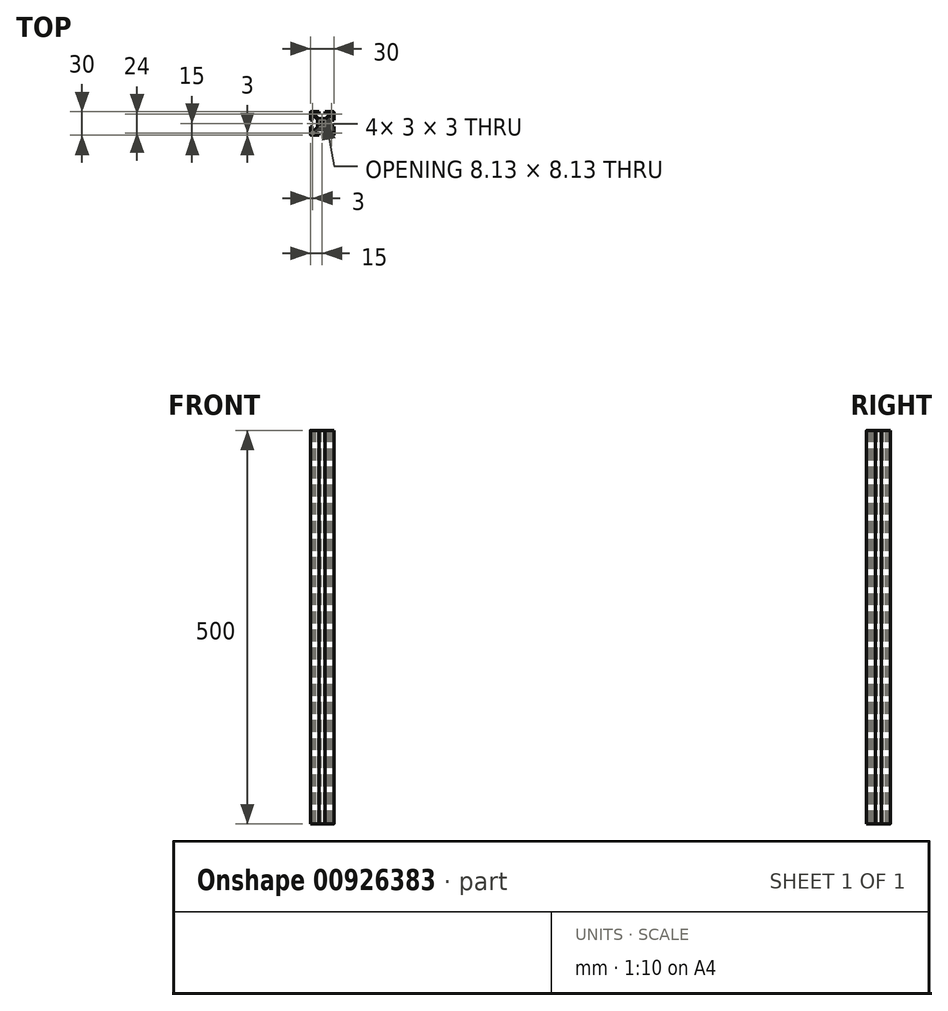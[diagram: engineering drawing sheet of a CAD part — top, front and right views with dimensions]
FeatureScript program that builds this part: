
annotation { "Feature Type Name" : "Feature", "Feature Type Description" : "" }
export const myFeature = defineFeature(function(context is Context, id is Id, definition is map)
    precondition{}
    {
        {
            var Q0;
            Q0=qCreatedBy(makeId("Top.planeOp"),FACE);
            var sketch = newSketch(context, id + "F0", { "sketchPlane" : qUnion([Q0])});
            skLineSegment(sketch, "E0", {"start": v(0, 0) * mm, "end": v(11, 0) * mm});
            skLineSegment(sketch, "E1", {"start": v(11, 0) * mm, "end": v(11, 2) * mm});
            skLineSegment(sketch, "E2", {"start": v(11, 2) * mm, "end": v(6, 2) * mm});
            skLineSegment(sketch, "E3", {"start": v(6, 2) * mm, "end": v(6, 4.59) * mm});
            skLineSegment(sketch, "E4", {"start": v(6, 4.59) * mm, "end": v(10.41, 9) * mm});
            skLineSegment(sketch, "E5", {"start": v(10.41, 9) * mm, "end": v(15, 9) * mm});
            skLineSegment(sketch, "E6", {"start": v(0, 0) * mm, "end": v(33.2, 33.2) * mm, "construction": true});
            skLineSegment(sketch, "E7", {"start": v(0, 15) * mm, "end": v(36.66, 15) * mm, "construction": true});
            skLineSegment(sketch, "E8", {"start": v(15, 0) * mm, "end": v(15, 32.9) * mm, "construction": true});
            skLineSegment(sketch, "E9", {"start": v(1.5, 1.5) * mm, "end": v(4.5, 1.5) * mm});
            skLineSegment(sketch, "E10", {"start": v(4.5, 1.5) * mm, "end": v(4.5, 4.5) * mm});
            skArc(sketch, "E11", {"start": v(13.19, 12.12) * mm, "mid": v(14.06, 11.73) * mm, "end": v(15, 11.6) * mm});
            skLineSegment(sketch, "E12", {"start": v(13.19, 12.12) * mm, "end": v(12, 10.93) * mm});
            skLineSegment(sketch, "E13", {"start": v(12, 10.93) * mm, "end": v(11.46, 11.46) * mm});
            skArc(sketch, "E14.MirrorCS", {"start": v(12.12, 13.19) * mm, "mid": v(11.73, 14.06) * mm, "end": v(11.6, 15) * mm});
            skLineSegment(sketch, "E15.MirrorCS", {"start": v(12.12, 13.19) * mm, "end": v(10.93, 12) * mm});
            skLineSegment(sketch, "E16.MirrorCS", {"start": v(10.93, 12) * mm, "end": v(11.46, 11.46) * mm});
            skLineSegment(sketch, "E17.MirrorCS", {"start": v(9, 10.41) * mm, "end": v(9, 15) * mm});
            skLineSegment(sketch, "E18.MirrorCS", {"start": v(4.59, 6) * mm, "end": v(9, 10.41) * mm});
            skLineSegment(sketch, "E19.MirrorCS", {"start": v(1.5, 4.5) * mm, "end": v(4.5, 4.5) * mm});
            skLineSegment(sketch, "E20.MirrorCS", {"start": v(1.5, 1.5) * mm, "end": v(1.5, 4.5) * mm});
            skLineSegment(sketch, "E21.MirrorCS", {"start": v(2, 11) * mm, "end": v(2, 6) * mm});
            skLineSegment(sketch, "E22.MirrorCS", {"start": v(0, 0) * mm, "end": v(0, 11) * mm});
            skLineSegment(sketch, "E23.MirrorCS", {"start": v(0, 11) * mm, "end": v(2, 11) * mm});
            skLineSegment(sketch, "E24.MirrorCS", {"start": v(2, 6) * mm, "end": v(4.59, 6) * mm});
            skLineSegment(sketch, "E25.MirrorCS", {"start": v(10.93, 18) * mm, "end": v(11.46, 18.54) * mm});
            skLineSegment(sketch, "E26.MirrorCS", {"start": v(12, 19.07) * mm, "end": v(11.46, 18.54) * mm});
            skLineSegment(sketch, "E27.MirrorCS", {"start": v(13.19, 17.88) * mm, "end": v(12, 19.07) * mm});
            skLineSegment(sketch, "E28.MirrorCS", {"start": v(11, 28) * mm, "end": v(6, 28) * mm});
            skLineSegment(sketch, "E29.MirrorCS", {"start": v(2, 19) * mm, "end": v(2, 24) * mm});
            skLineSegment(sketch, "E30.MirrorCS", {"start": v(12.12, 16.81) * mm, "end": v(10.93, 18) * mm});
            skLineSegment(sketch, "E31.MirrorCS", {"start": v(2, 24) * mm, "end": v(4.59, 24) * mm});
            skLineSegment(sketch, "E32.MirrorCS", {"start": v(4.59, 24) * mm, "end": v(9, 19.59) * mm});
            skLineSegment(sketch, "E33.MirrorCS", {"start": v(1.5, 28.5) * mm, "end": v(4.5, 28.5) * mm});
            skLineSegment(sketch, "E34.MirrorCS", {"start": v(0, 30) * mm, "end": v(0, 19) * mm});
            skLineSegment(sketch, "E35.MirrorCS", {"start": v(1.5, 28.5) * mm, "end": v(1.5, 25.5) * mm});
            skLineSegment(sketch, "E36.MirrorCS", {"start": v(10.41, 21) * mm, "end": v(15, 21) * mm});
            skArc(sketch, "E37.MirrorCS", {"start": v(13.19, 17.88) * mm, "mid": v(14.06, 18.27) * mm, "end": v(15, 18.4) * mm});
            skLineSegment(sketch, "E38.MirrorCS", {"start": v(1.5, 25.5) * mm, "end": v(4.5, 25.5) * mm});
            skLineSegment(sketch, "E39.MirrorCS", {"start": v(0, 19) * mm, "end": v(2, 19) * mm});
            skArc(sketch, "E40.MirrorCS", {"start": v(12.12, 16.81) * mm, "mid": v(11.73, 15.94) * mm, "end": v(11.6, 15) * mm});
            skLineSegment(sketch, "E41.MirrorCS", {"start": v(11, 30) * mm, "end": v(11, 28) * mm});
            skLineSegment(sketch, "E42.MirrorCS", {"start": v(6, 25.41) * mm, "end": v(10.41, 21) * mm});
            skLineSegment(sketch, "E43.MirrorCS", {"start": v(4.5, 28.5) * mm, "end": v(4.5, 25.5) * mm});
            skLineSegment(sketch, "E44.MirrorCS", {"start": v(6, 28) * mm, "end": v(6, 25.41) * mm});
            skLineSegment(sketch, "E45.MirrorCS", {"start": v(0, 30) * mm, "end": v(11, 30) * mm});
            skLineSegment(sketch, "E46.MirrorCS", {"start": v(9, 19.59) * mm, "end": v(9, 15) * mm});
            skLineSegment(sketch, "E47.MirrorCS", {"start": v(18, 10.93) * mm, "end": v(18.54, 11.46) * mm});
            skLineSegment(sketch, "E48.MirrorCS", {"start": v(16.81, 17.88) * mm, "end": v(18, 19.07) * mm});
            skLineSegment(sketch, "E49.MirrorCS", {"start": v(19.07, 18) * mm, "end": v(18.54, 18.54) * mm});
            skLineSegment(sketch, "E50.MirrorCS", {"start": v(17.88, 16.81) * mm, "end": v(19.07, 18) * mm});
            skLineSegment(sketch, "E51.MirrorCS", {"start": v(17.88, 13.19) * mm, "end": v(19.07, 12) * mm});
            skLineSegment(sketch, "E52.MirrorCS", {"start": v(16.81, 12.12) * mm, "end": v(18, 10.93) * mm});
            skLineSegment(sketch, "E53.MirrorCS", {"start": v(18, 19.07) * mm, "end": v(18.54, 18.54) * mm});
            skLineSegment(sketch, "E54.MirrorCS", {"start": v(19.07, 12) * mm, "end": v(18.54, 11.46) * mm});
            skLineSegment(sketch, "E55.MirrorCS", {"start": v(25.5, 1.5) * mm, "end": v(25.5, 4.5) * mm});
            skLineSegment(sketch, "E56.MirrorCS", {"start": v(24, 2) * mm, "end": v(24, 4.59) * mm});
            skLineSegment(sketch, "E57.MirrorCS", {"start": v(24, 4.59) * mm, "end": v(19.59, 9) * mm});
            skLineSegment(sketch, "E58.MirrorCS", {"start": v(24, 25.41) * mm, "end": v(19.59, 21) * mm});
            skLineSegment(sketch, "E59.MirrorCS", {"start": v(24, 28) * mm, "end": v(24, 25.41) * mm});
            skArc(sketch, "E60.MirrorCS", {"start": v(17.88, 13.19) * mm, "mid": v(18.27, 14.06) * mm, "end": v(18.4, 15) * mm});
            skArc(sketch, "E61.MirrorCS", {"start": v(16.81, 17.88) * mm, "mid": v(15.94, 18.27) * mm, "end": v(15, 18.4) * mm});
            skLineSegment(sketch, "E62.MirrorCS", {"start": v(28, 24) * mm, "end": v(25.41, 24) * mm});
            skLineSegment(sketch, "E63.MirrorCS", {"start": v(25.5, 28.5) * mm, "end": v(25.5, 25.5) * mm});
            skLineSegment(sketch, "E64.MirrorCS", {"start": v(28.5, 1.5) * mm, "end": v(28.5, 4.5) * mm});
            skLineSegment(sketch, "E65.MirrorCS", {"start": v(21, 10.41) * mm, "end": v(21, 15) * mm});
            skLineSegment(sketch, "E66.MirrorCS", {"start": v(28, 11) * mm, "end": v(28, 6) * mm});
            skLineSegment(sketch, "E67.MirrorCS", {"start": v(21, 19.59) * mm, "end": v(21, 15) * mm});
            skLineSegment(sketch, "E68.MirrorCS", {"start": v(30, 0) * mm, "end": v(19, 0) * mm});
            skArc(sketch, "E69.MirrorCS", {"start": v(17.88, 16.81) * mm, "mid": v(18.27, 15.94) * mm, "end": v(18.4, 15) * mm});
            skLineSegment(sketch, "E70.MirrorCS", {"start": v(28.5, 25.5) * mm, "end": v(25.5, 25.5) * mm});
            skLineSegment(sketch, "E71.MirrorCS", {"start": v(28.5, 28.5) * mm, "end": v(25.5, 28.5) * mm});
            skLineSegment(sketch, "E72.MirrorCS", {"start": v(30, 30) * mm, "end": v(30, 19) * mm});
            skLineSegment(sketch, "E73.MirrorCS", {"start": v(28.5, 28.5) * mm, "end": v(28.5, 25.5) * mm});
            skLineSegment(sketch, "E74.MirrorCS", {"start": v(19.59, 9) * mm, "end": v(15, 9) * mm});
            skLineSegment(sketch, "E75.MirrorCS", {"start": v(19, 0) * mm, "end": v(19, 2) * mm});
            skLineSegment(sketch, "E76.MirrorCS", {"start": v(30, 0) * mm, "end": v(30, 11) * mm});
            skLineSegment(sketch, "E77.MirrorCS", {"start": v(25.41, 6) * mm, "end": v(21, 10.41) * mm});
            skLineSegment(sketch, "E78.MirrorCS", {"start": v(25.41, 24) * mm, "end": v(21, 19.59) * mm});
            skLineSegment(sketch, "E79.MirrorCS", {"start": v(19.59, 21) * mm, "end": v(15, 21) * mm});
            skLineSegment(sketch, "E80.MirrorCS", {"start": v(19, 30) * mm, "end": v(19, 28) * mm});
            skLineSegment(sketch, "E81.MirrorCS", {"start": v(30, 19) * mm, "end": v(28, 19) * mm});
            skLineSegment(sketch, "E82.MirrorCS", {"start": v(30, 11) * mm, "end": v(28, 11) * mm});
            skLineSegment(sketch, "E83.MirrorCS", {"start": v(19, 28) * mm, "end": v(24, 28) * mm});
            skLineSegment(sketch, "E84.MirrorCS", {"start": v(28, 6) * mm, "end": v(25.41, 6) * mm});
            skLineSegment(sketch, "E85.MirrorCS", {"start": v(28.5, 4.5) * mm, "end": v(25.5, 4.5) * mm});
            skLineSegment(sketch, "E86.MirrorCS", {"start": v(28, 19) * mm, "end": v(28, 24) * mm});
            skLineSegment(sketch, "E87.MirrorCS", {"start": v(19, 2) * mm, "end": v(24, 2) * mm});
            skLineSegment(sketch, "E88.MirrorCS", {"start": v(28.5, 1.5) * mm, "end": v(25.5, 1.5) * mm});
            skLineSegment(sketch, "E89.MirrorCS", {"start": v(30, 30) * mm, "end": v(19, 30) * mm});
            skArc(sketch, "E90.MirrorCS", {"start": v(16.81, 12.12) * mm, "mid": v(15.94, 11.73) * mm, "end": v(15, 11.6) * mm});
            skSolve(sketch);
        }
        {
            var Q0;
            Q0=qSketchRegion(id+"F0",true);
            extrude(context, id + "F1", {"entities" : qUnion([Q0]), "depth" : 500 * mm, "offsetDistance" : 25 * mm});
        }
        {
            var Q0;
            Q0=makeQuery(id+"F1.opExtrude","SWEPT_EDGE",EDGE,{"disambiguationData":[OSD([sQuery(id+"F0.wireOp",EDGE,"E34.MirrorCS"),sQuery(id+"F0.wireOp",EDGE,"E45.MirrorCS")])]});
            var Q1;
            Q1=makeQuery(id+"F1.opExtrude","SWEPT_EDGE",EDGE,{"disambiguationData":[OSD([sQuery(id+"F0.wireOp",EDGE,"E72.MirrorCS"),sQuery(id+"F0.wireOp",EDGE,"E89.MirrorCS")])]});
            var Q2;
            Q2=makeQuery(id+"F1.opExtrude","SWEPT_EDGE",EDGE,{"disambiguationData":[OSD([sQuery(id+"F0.wireOp",EDGE,"E68.MirrorCS"),sQuery(id+"F0.wireOp",EDGE,"E76.MirrorCS")])]});
            var Q3;
            Q3=makeQuery(id+"F1.opExtrude","SWEPT_EDGE",EDGE,{"disambiguationData":[OSD([sQuery(id+"F0.wireOp",EDGE,"E0"),sQuery(id+"F0.wireOp",EDGE,"E22.MirrorCS")])]});
            fillet(context, id + "F2", {"entities" : qUnion([Q0, Q1, Q2, Q3]), "radius" : 1 * mm, "tangentPropagation" : true, "allowEdgeOverflow" : false});
        }
    });
